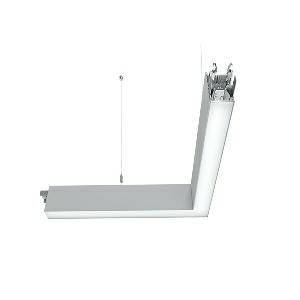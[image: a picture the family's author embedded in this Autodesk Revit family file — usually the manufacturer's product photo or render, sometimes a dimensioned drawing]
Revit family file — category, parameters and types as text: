
# Revit family: idoo_line_-_ilp_3000_vtl_d_ll_mid_00807710_8fba
name_source: partatom
category: Lighting Fixtures
units: mm (PartAtom-declared; Revit-internal decimal feet)

## family parameters
Cut with Voids When Loaded = No
Host = Face
Light Source = No
Part Type = Normal
Room Calculation Point = No
Round Connector Dimension = Use Diameter
Shared = No

## types (1)
- IDOO.line - ILP 3000/VTL/D/LL MID (1 x LED, 3150 lm, 2700-6500K)
    Apparent Load = 32 VA
    Approval mark = CE
    CIE Flux Codes = 66 91 98 40 100
    Color Rendering = 90-100
    Color Temperature = 2700-6500K
    Control Gear = Electronic ballast
    Default Elevation = 1800 mm
    Description = ILP 3000/VTL/D|Suspended luminaire|light source: LED|connected load: 220-240 V, 50/60 Hz|Power consumption: approx. 32 W|standby: approx. 0,25|luminous flux: 3150 lm|luminous efficacy: 98 lm/W|light distribution: Direct/indirect|direct ratio: approx. 40 %|colour temperature: Cold white, ca. 2700-6500 K|color rendering index (CRI): >= 90|chromaticity tolerance:  3 SDCM|System of protection: IP 40|technology: Continuously dimmable|luminaire body|material: Sectional aluminium|colour: Silver|lamp cover: Acrylic (PMMA), Clear|Fastening: Steel cable 0.3 - 0.7 m|glare control: Prism aperture|luminance(L65): <= 2700 cd/m|unified glare rating(4H 8H): <=  16|special features: Specified values at approx. 4000 K, DALI Load 1x, Through-wired, up to 18 m on one mains connection, External control required for Dali Device type 8, Flicker-free, Constant luminous flux between 2700 and 6500 K, Constant colour temperature over the whole dimming range, Continous light without dark z, 90░ rerouting on the left side, Suitable as emergency lighting, Mechanical and electrical connection of the individual modules without tools|
    Frequency = 50 Hz
    Height = 110 mm
    Lamp = 1 x LED
    Lamp Light Flux = 3150 lm
    Lamp count = 1
    Length = 600 mm
    Luminous efficacy = 98 lm/W
    Manufacturer = Waldmann
    ModVariant = No
    Model = 00807710
    Mounting Place = Ceiling
    Mounting Type = Pendant
    Number of Poles = 1
    OnlyDefault = Yes
    Power Factor = 1
    Product Name = IDOO.line - ILP 3000/VTL/D/LL MID
    Product group = Suspended luminaire
    ProductGroupID = 9
    Protection Class = Protection class I
    Protection Degree = IP 40
    RLX_Detail_Level = 1
    RLX_Emergency_Light_Flux = 0 lm
    RLX_Emergency_Type = 0
    RLX_Emergency_Type_DB = No
    RlxData = <blob elided: 22041 chars, md5=c6f62c1c>
    Socket = socket
    Standby Power = 0 W
    System Light Flux = 3150 lm
    System Power = 32 W
    Type Comments = Product without accessories
    Type Image = ilp_dlp_ll_si.jpg
    URL = http://relux.com
    VarID = ---
    Voltage = 230 V
    Voltage Range = 220-240 V
    Weight = 0.00 kg
    Width = 600 mm

## geometry (parser evidence)
native form markers: Blend x4, Sweep x14
no freeform markers — native parametric forms only
